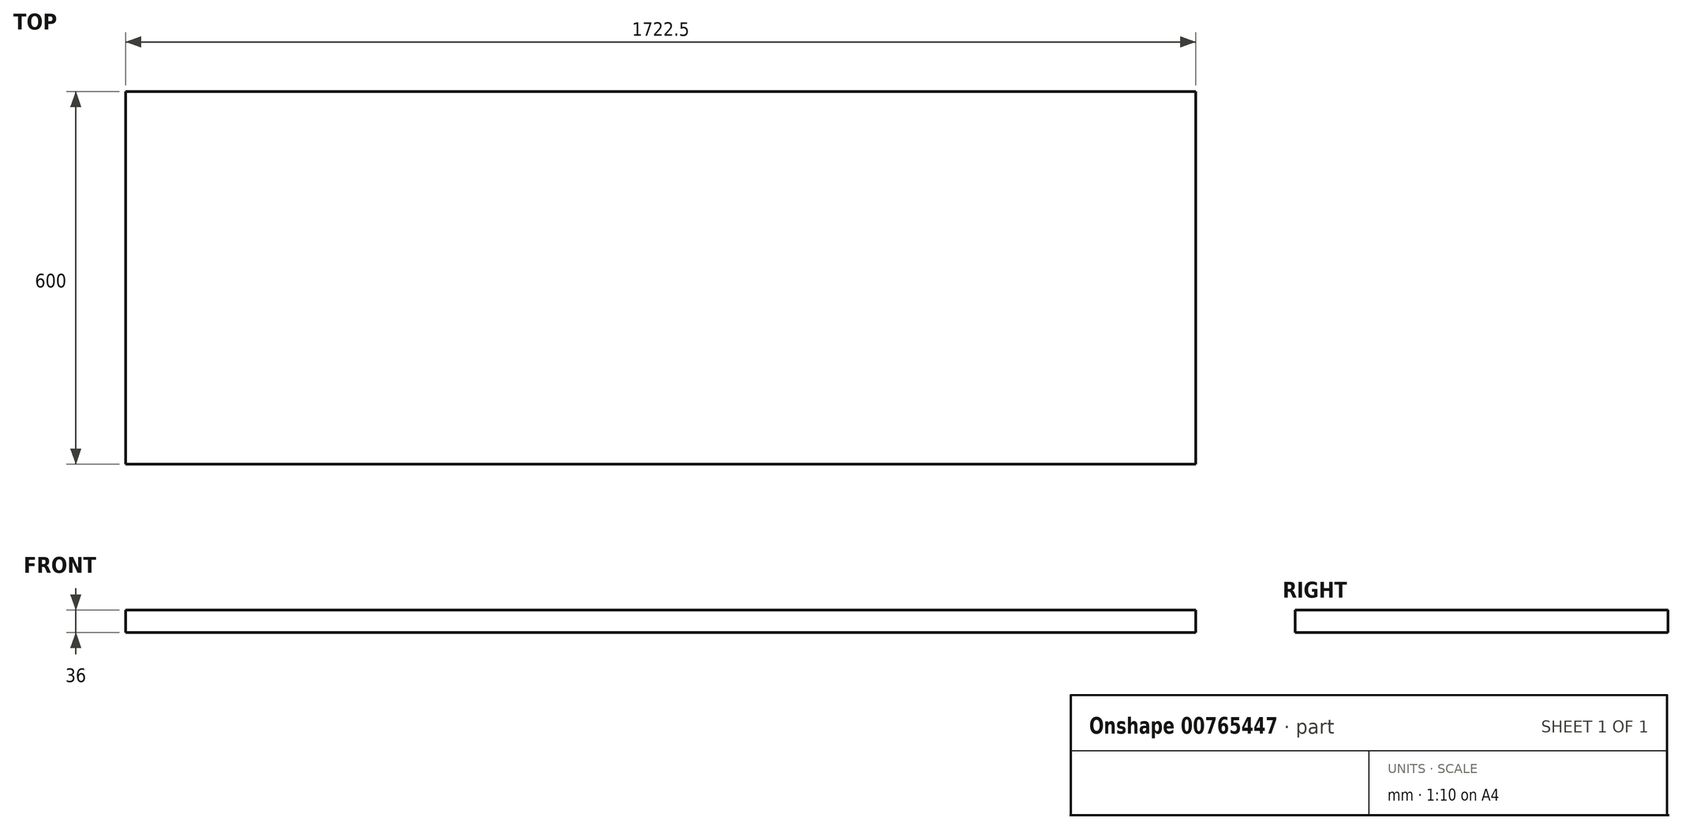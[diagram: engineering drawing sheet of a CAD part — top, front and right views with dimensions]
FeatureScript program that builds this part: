
annotation { "Feature Type Name" : "Feature", "Feature Type Description" : "" }
export const myFeature = defineFeature(function(context is Context, id is Id, definition is map)
    precondition{}
    {
        {
            var Q0;
            Q0=qCreatedBy(makeId("Top.planeOp"),FACE);
            var sketch = newSketch(context, id + "F0", { "sketchPlane" : qUnion([Q0])});
            skLineSegment(sketch, "E0.bottom", {"start": v(-861.25, -300) * mm, "end": v(861.25, -300) * mm});
            skLineSegment(sketch, "E0.top", {"start": v(-861.25, 300) * mm, "end": v(861.25, 300) * mm});
            skLineSegment(sketch, "E0.left", {"start": v(-861.25, -300) * mm, "end": v(-861.25, 300) * mm});
            skLineSegment(sketch, "E0.right", {"start": v(861.25, -300) * mm, "end": v(861.25, 300) * mm});
            skPoint(sketch, "E0.middle", {"position": v(0, 0) * mm});
            skSolve(sketch);
        }
        {
            var Q0;
            Q0 = qSketchRegion(id + "F0", true);
            extrude(context, id + "F1", {"entities" : qUnion([Q0]), "depth" : 36 * mm, "offsetDistance" : 25 * mm});
        }
    });
